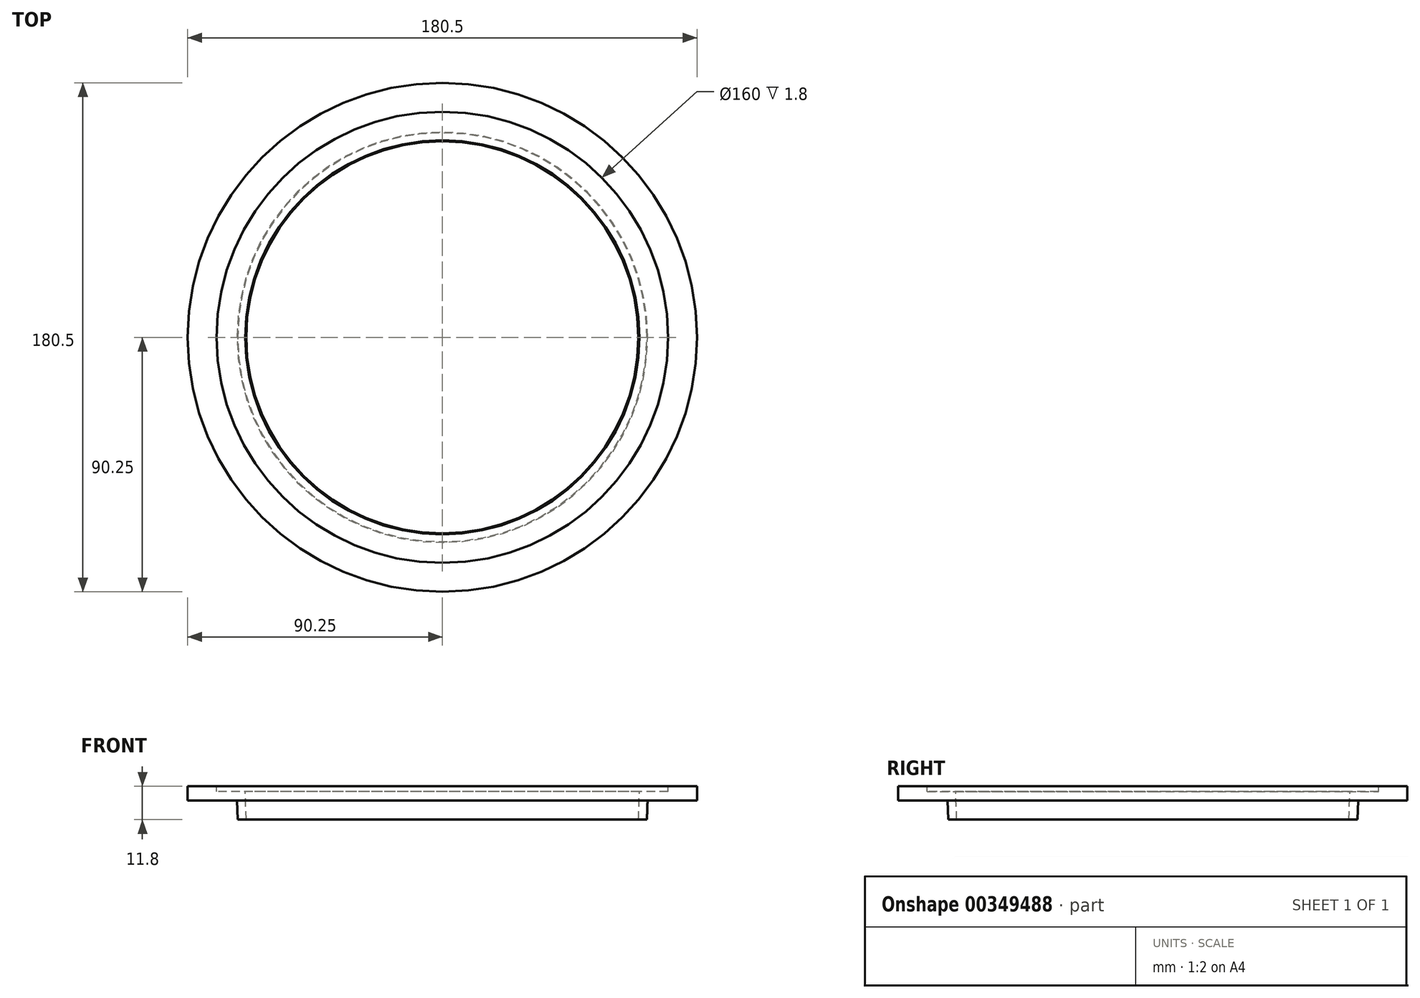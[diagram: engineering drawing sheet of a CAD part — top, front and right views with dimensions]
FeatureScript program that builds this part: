
annotation { "Feature Type Name" : "Feature", "Feature Type Description" : "" }
export const myFeature = defineFeature(function(context is Context, id is Id, definition is map)
    precondition{}
    {
        {
            var Q0;
            Q0=qCreatedBy(makeId("Right.planeOp"),FACE);
            var sketch = newSketch(context, id + "F0", { "sketchPlane" : qUnion([Q0])});
            skLineSegment(sketch, "E0", {"start": v(0, 38.05) * mm, "end": v(0, -38.05) * mm, "construction": true});
            skLineSegment(sketch, "E1", {"start": v(90.25, 5) * mm, "end": v(80, 5) * mm});
            skLineSegment(sketch, "E2", {"start": v(80, 5) * mm, "end": v(80, 3.2) * mm});
            skLineSegment(sketch, "E3", {"start": v(80, 3.2) * mm, "end": v(69.86, 3.2) * mm});
            skLineSegment(sketch, "E4", {"start": v(90.25, 5) * mm, "end": v(90.25, 0) * mm});
            skLineSegment(sketch, "E5", {"start": v(90.25, 0) * mm, "end": v(72.75, 0) * mm});
            skLineSegment(sketch, "E6", {"start": v(72.75, 0) * mm, "end": v(72.51, -6.8) * mm});
            skLineSegment(sketch, "E7", {"start": v(72.51, -6.8) * mm, "end": v(69.51, -6.8) * mm});
            skLineSegment(sketch, "E8", {"start": v(69.86, 3.2) * mm, "end": v(69.51, -6.8) * mm});
            skSolve(sketch);
        }
        {
            var Q0;
            Q0 = qSketchRegion(id + "F0", true);
            var Q1;
            Q1=sQuery(id+"F0.wireOp",EDGE,"E0");
            revolve(context, id + "F1", {"entities" : qUnion([Q0]), "axis" : qUnion([Q1]), "revolveType" : RevolveType.FULL});
        }
        {
            var Q0;
            Q0=qCreatedBy(makeId("Right.planeOp"),FACE);
            var sketch = newSketch(context, id + "F2", { "sketchPlane" : qUnion([Q0])});
            skLineSegment(sketch, "E9", {"start": v(0, 0) * mm, "end": v(0, -71.38) * mm, "construction": true});
            skLineSegment(sketch, "E10", {"start": v(56.5, -28.5) * mm, "end": v(56.5, -34) * mm});
            skLineSegment(sketch, "E11", {"start": v(56.5, -34) * mm, "end": v(48.5, -34.28) * mm});
            skLineSegment(sketch, "E12", {"start": v(56.5, -28.5) * mm, "end": v(54.5, -28.5) * mm});
            skLineSegment(sketch, "E13", {"start": v(54.5, -28.5) * mm, "end": v(54.37, -32.28) * mm});
            skLineSegment(sketch, "E14", {"start": v(54.37, -32.28) * mm, "end": v(45.57, -32.28) * mm});
            skLineSegment(sketch, "E15", {"start": v(48.5, -34.28) * mm, "end": v(48.2, -43) * mm});
            skLineSegment(sketch, "E16", {"start": v(48.2, -43) * mm, "end": v(45.2, -43) * mm});
            skLineSegment(sketch, "E17", {"start": v(45.57, -32.28) * mm, "end": v(45.2, -43) * mm});
            skSolve(sketch);
        }
        {
            var Q0;
            Q0 = qConstructionFilter(qBodyType(qCreatedBy(id + "F2" ,EDGE), BodyType.WIRE), ConstructionObject.NO);
            var Q1;
            Q1=sQuery(id+"F2.wireOp",EDGE,"E9");
            revolve(context, id + "F3", {"bodyType" : ToolBodyType.SURFACE, "surfaceEntities" : qUnion([Q0]), "axis" : qUnion([Q1]), "revolveType" : RevolveType.FULL});
        }
        {
            var Q0;
            Q0=makeQuery(id+"F3.opRevolve","SWEPT_EDGE",EDGE,{"disambiguationData":[OSD([sQuery(id+"F2.wireOp",VERTEX,"E11.start")])]});
            var Q1;
            Q1=makeQuery(id+"F3.opRevolve","SWEPT_EDGE",EDGE,{"disambiguationData":[OSD([sQuery(id+"F2.wireOp",VERTEX,"E15.start")])]});
            var Q2;
            Q2=makeQuery(id+"F3.opRevolve","SWEPT_EDGE",EDGE,{"disambiguationData":[OSD([sQuery(id+"F2.wireOp",VERTEX,"E16.start")])]});
            var Q3;
            Q3=makeQuery(id+"F3.opRevolve","SWEPT_EDGE",EDGE,{"disambiguationData":[OSD([sQuery(id+"F2.wireOp",VERTEX,"E14.start")])]});
            fillet(context, id + "F4", {"entities" : qUnion([Q0, Q1, Q2, Q3]), "radius" : 2.5 * mm, "tangentPropagation" : true, "allowEdgeOverflow" : false});
        }
        {
            var Q0;
            Q0=makeQuery(id+"F3.opRevolve","SWEPT_FACE",FACE,{"disambiguationData":[OSD([sQuery(id+"F2.wireOp",EDGE,"E12")])]});
            cPlane(context, id + "F5", {"entities" : qUnion([Q0]), "cplaneType" : CPlaneType.OFFSET, "offset" : 1.5 * mm, "width" : 150 * mm, "height" : 150 * mm});
        }
    });
